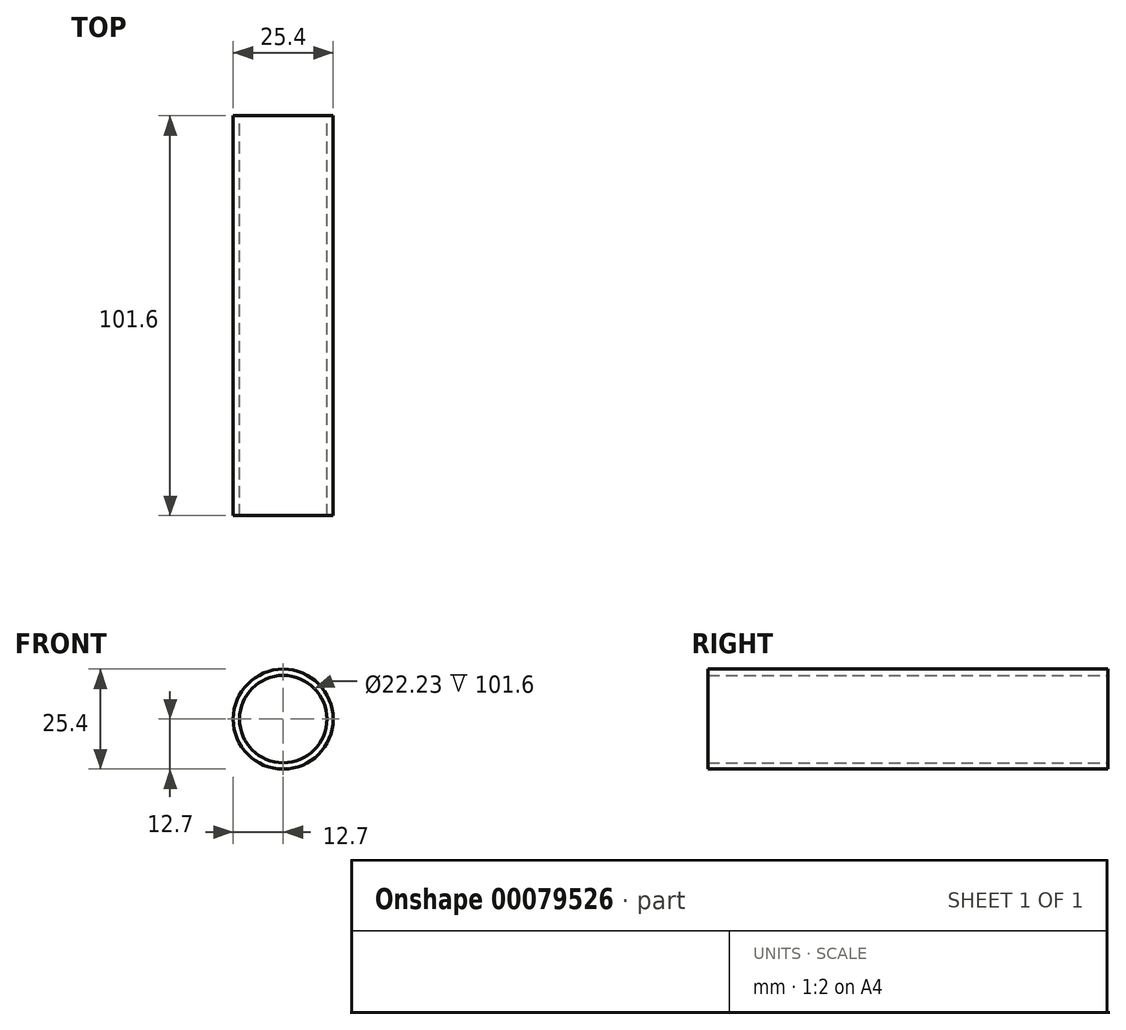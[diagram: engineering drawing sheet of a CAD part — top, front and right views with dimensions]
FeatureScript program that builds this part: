
annotation { "Feature Type Name" : "Feature", "Feature Type Description" : "" }
export const myFeature = defineFeature(function(context is Context, id is Id, definition is map)
    precondition{}
    {
        {
            var Q0;
            Q0=qCreatedBy(makeId("Front.planeOp"),FACE);
            var sketch = newSketch(context, id + "F0", { "sketchPlane" : qUnion([Q0])});
            skCircle(sketch, "E0", {"center": v(0, 0) * mm, "radius": 12.7 * mm});
            skCircle(sketch, "E1", {"center": v(0, 0) * mm, "radius": 11.11 * mm});
            skSolve(sketch);
        }
        {
            var Q0;
            Q0=makeQuery(id+"F0.imprint","IMPRINT",FACE,{"disambiguationData":[TD([[makeQuery(id+"F0.imprint","IMPRINT",EDGE,{"derivedFrom":sQuery(id+"F0.wireOp",EDGE,"E0")}),1.0]])]});
            extrude(context, id + "F1", {"entities" : qUnion([Q0]), "depth" : 101.6 * mm});
        }
    });
